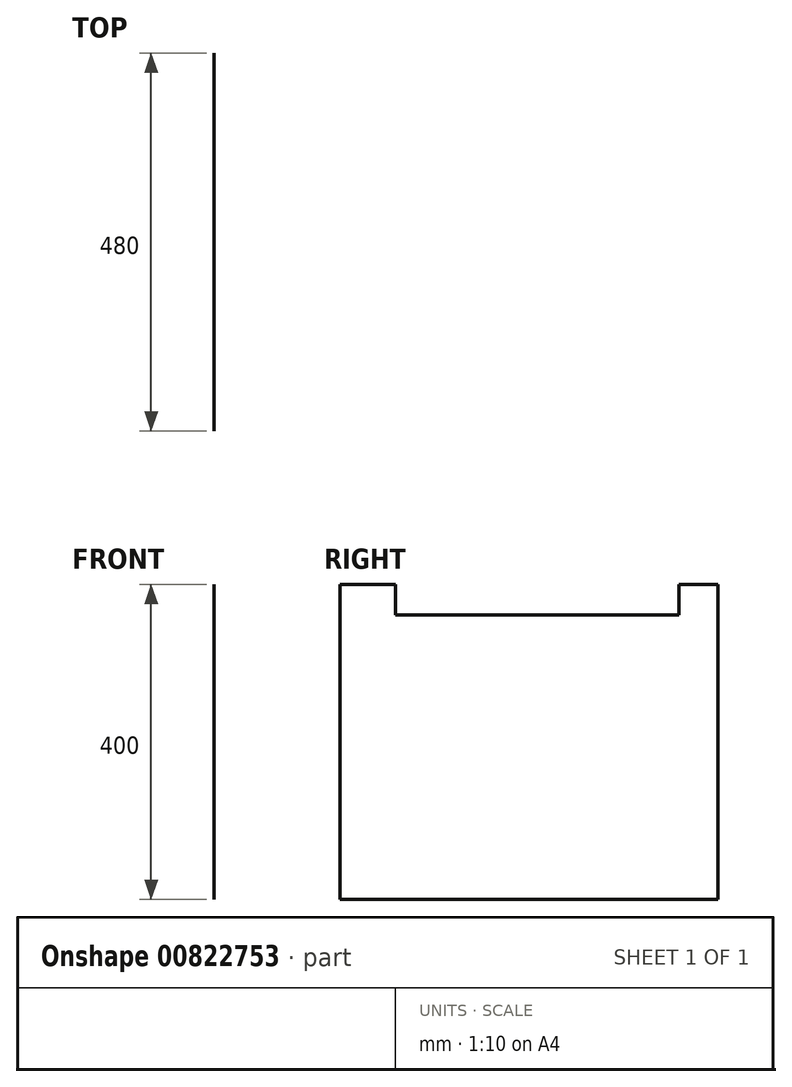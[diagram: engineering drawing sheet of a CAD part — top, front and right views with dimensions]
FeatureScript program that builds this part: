
annotation { "Feature Type Name" : "Feature", "Feature Type Description" : "" }
export const myFeature = defineFeature(function(context is Context, id is Id, definition is map)
    precondition{}
    {
        {
            var Q0;
            Q0=qCreatedBy(makeId("Right.planeOp"),FACE);
            var sketch = newSketch(context, id + "F0", { "sketchPlane" : qUnion([Q0])});
            skLineSegment(sketch, "E0.bottom", {"start": v(-240, -200) * mm, "end": v(240, -200) * mm});
            skLineSegment(sketch, "E0.left", {"start": v(-240, -200) * mm, "end": v(-240, 200) * mm});
            skLineSegment(sketch, "E0.right", {"start": v(240, -200) * mm, "end": v(240, 200) * mm});
            skPoint(sketch, "E0.middle", {"position": v(0, 0) * mm});
            skLineSegment(sketch, "E1", {"start": v(0, -200) * mm, "end": v(0, 200) * mm, "construction": true});
            skLineSegment(sketch, "E2", {"start": v(-240, 200) * mm, "end": v(-170, 200) * mm});
            skLineSegment(sketch, "E3", {"start": v(-170, 200) * mm, "end": v(-170, 161.35) * mm});
            skLineSegment(sketch, "E4", {"start": v(-170, 161.35) * mm, "end": v(190, 161.35) * mm});
            skLineSegment(sketch, "E5", {"start": v(190, 161.35) * mm, "end": v(190, 200) * mm});
            skLineSegment(sketch, "E6.trimOffspring", {"start": v(190, 200) * mm, "end": v(240, 200) * mm});
            skSolve(sketch);
        }
        {
            var Q0;
            Q0=makeQuery(id+"F0.imprint","IMPRINT",FACE,{"disambiguationData":[TD([[makeQuery(id+"F0.imprint","IMPRINT",EDGE,{"derivedFrom":sQuery(id+"F0.wireOp",EDGE,"E0.bottom")}),1.0]])]});
            extrude(context, id + "F1", {"entities" : qUnion([Q0]), "depth" : 1 / 406.4 * mm, "offsetDistance" : 25 * mm});
        }
    });
